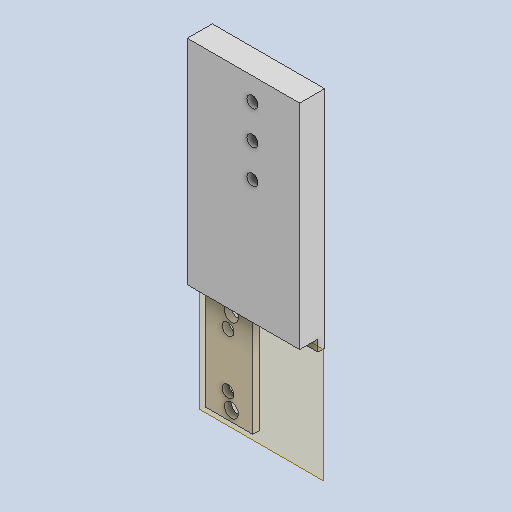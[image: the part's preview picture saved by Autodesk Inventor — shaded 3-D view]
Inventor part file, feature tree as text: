
AUTODESK INVENTOR PART (.ipt)
format: ipt  version: 2022 (Build 260153000, 153)  size: 155,136 bytes
history: native  units: in
note: dims shown in document units (in); Inventor stores cm internally (conversion verified against a paired STEP export)
features: other x5, sketch x4, extrude x2, reference x2, plane x1
ambient origin geometry x8: Origin, YZ Plane, XZ Plane, XY Plane, X Axis, Y Axis, Z Axis, Center Point
bodies: Solid1 (feature_tree)
feature tree (14):
  other  "endcap insert.ipt"
  extrude  "Extrusion1"  Depth=0.3937in
  extrude  "Extrusion2"  TaperAngle=0.0deg  [1 undecoded]
  other  "Solid1::endcap insert.ipt"
  other  "TaggingFeature1"
  sketch  "Sketch1"  dims[d0=0.3937in d1=0.0039in]
  sketch  "Sketch3"  dims[d2=0.3937in d3=0.0in d4=0.0in d5=0.0in]
  plane  "Work Plane1"
  sketch  "Sketch4"
  reference  "Reference1"
  sketch  "Sketch5"
  reference  "Reference2"
  other  "Linear Rail Assembly.iam"
  other  "Linear Rail Front Plate:1"
note: 1 required parameter value undecoded (feature->parameter linkage not recoverable at this tier; creation-order binding heuristic only, values carry confidence <= 0.55)
